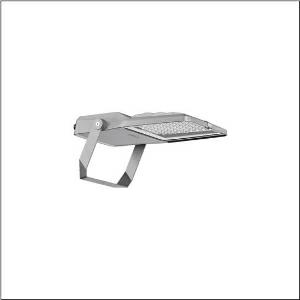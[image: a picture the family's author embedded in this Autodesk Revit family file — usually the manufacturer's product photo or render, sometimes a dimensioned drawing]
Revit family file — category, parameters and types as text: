
# Revit family: floodlight_fl_21_mini___pl52_5xa7776c4d1a_cdf3
name_source: partatom
category: Lighting Fixtures
units: mm (PartAtom-declared; Revit-internal decimal feet)

## family parameters
Cut with Voids When Loaded = No
Host = Face
Light Source = No
Part Type = Normal
Room Calculation Point = No
Round Connector Dimension = Use Diameter
Shared = No

## types (1)
- --- (1 x LED, 12700 lm, 89 W, 4000K)
    Apparent Load = 89 VA
    CIE Flux Codes = 26 60 98 100 100
    Color Rendering = 70
    Color Temperature = 4000K
    Default Elevation = 1800 mm
    Description = Floodlight FL 21 mini, floodlight, primary light control with lens, of PMMA, primary optical cover: protective disc, of toughened safety glass, transparent, light distribution: PL52, light emission: direct distribution, installation type: surface-mounted, LED, High Power LED, rated luminous flux: 12.700lm, luminous efficacy: 143lm/W, light colour: 740, colour temperature: 4000K, control gear: D4iSmart Interface (Zhaga), control: overheat protection, constant luminous flux control, time-dependent luminous flux control, flexible luminous flux parameterisation, pre-setting: logarithmic dimming characteristic, with terminal, 6-pole, mains connection: 220..240V, AC, 50/60Hz, start of lifetime: 89W, end of service life: 94W, reduction: 43W, mounting bracket, of diecast aluminium, powder-coated, Siteco® metallic grey (DB 702S), corrosivity category C5 mid according to DIN EN ISO 12944, suitable for swimming pools, chlorine-resistant, sealing non-destructively replaceable, mounting bracket, of steel, galvanised, powder-coated, Siteco® metallic grey (DB 702S), Smart Interface below and above, protection rating (complete): IP66, insulation class (complete): insulation class II (safety insulation), certification: CE, ENEC, VDE, protection symbol: D, impact resistance: IK08, permissible operating ambient temperature: -40..+40°C, permissible operating ambient temperature for outdoor applications: -40..+50°C, standard: DIN EN 12944, LABS conformity tested according to VDMA 24364:2018-05, packaging unit: 1 piece

Light Distribution: PL52
    Height = 70 mm
    Lamp = 1 x LED
    Lamp Light Flux = 12700 lm
    Lamp Power = 89 W
    Lamp count = 1
    Length = 485 mm
    Luminous efficacy = 143 lm/W
    Manufacturer = Siteco
    ModVariant = No
    Model = 5XA7776C4D1A
    Number of Poles = 1
    OnlyDefault = Yes
    Power Factor = 1
    Product Name = Floodlight FL 21 mini | PL52
    Product group = floodlight | pylon annexe
    ProductGroupID = 6200
    Protection Class = Protection class II
    Protection Degree = IP 66
    RLX_Detail_Level = 1
    RLX_Emergency_Light_Flux = 0 lm
    RLX_Emergency_Type = 0
    RLX_Emergency_Type_DB = No
    RlxData = <blob elided: 96165 chars, md5=6254b309>
    Socket = socket
    Standby Power = 0 W
    System Light Flux = 12700 lm
    System Power = 89 W
    Type Comments = factory setting: luminous flux: 100 % | dim-lin: 254 | 456 mA
    Type Image = l_1006845.jpg
    URL = http://relux.com
    VarID = @adj_095408
    Voltage = 0 V
    Weight = 0.00 kg
    Width = 337 mm

## geometry (parser evidence)
native form markers: Blend x4, Sweep x12
no freeform markers — native parametric forms only
